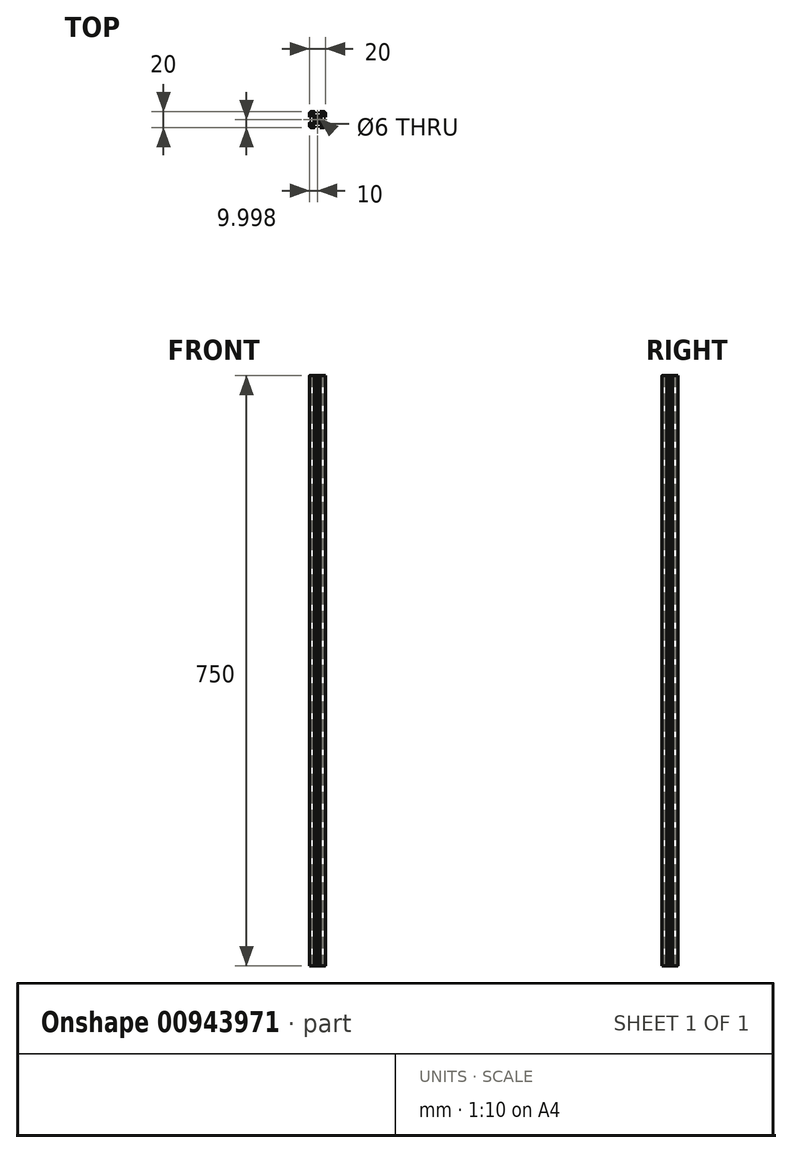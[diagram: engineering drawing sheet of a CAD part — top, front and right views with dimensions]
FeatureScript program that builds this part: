
annotation { "Feature Type Name" : "Feature", "Feature Type Description" : "" }
export const myFeature = defineFeature(function(context is Context, id is Id, definition is map)
    precondition{}
    {
        {
            var Q0;
            Q0=qCreatedBy(makeId("Top.planeOp"),FACE);
            var sketch = newSketch(context, id + "F0", { "sketchPlane" : qUnion([Q0])});
            skLineSegment(sketch, "E0.bottom", {"start": v(-8, -10) * mm, "end": v(8, -10) * mm});
            skLineSegment(sketch, "E0.top", {"start": v(-8, 10) * mm, "end": v(8, 10) * mm});
            skLineSegment(sketch, "E0.left", {"start": v(-10, -8) * mm, "end": v(-10, 8) * mm});
            skLineSegment(sketch, "E0.right", {"start": v(10, -8) * mm, "end": v(10, 8) * mm});
            skPoint(sketch, "E1.visualSharp", {"position": v(10, 10) * mm});
            skArc(sketch, "E1.filletArc", {"start": v(10, 8) * mm, "mid": v(9.41, 9.42) * mm, "end": v(8, 10) * mm});
            skPoint(sketch, "E2.visualSharp", {"position": v(-10, 10) * mm});
            skArc(sketch, "E2.filletArc", {"start": v(-8, 10) * mm, "mid": v(-9.41, 9.42) * mm, "end": v(-10, 8) * mm});
            skPoint(sketch, "E3.visualSharp", {"position": v(-10, -10) * mm});
            skArc(sketch, "E3.filletArc", {"start": v(-10, -8) * mm, "mid": v(-9.41, -9.4) * mm, "end": v(-8, -10) * mm});
            skPoint(sketch, "E4.visualSharp", {"position": v(10, -10) * mm});
            skArc(sketch, "E4.filletArc", {"start": v(8, -10) * mm, "mid": v(9.41, -9.4) * mm, "end": v(10, -8) * mm});
            skLineSegment(sketch, "E5", {"start": v(-10, -10) * mm, "end": v(10, 10) * mm, "construction": true});
            skLineSegment(sketch, "E6", {"start": v(-10, 10) * mm, "end": v(10, -10) * mm, "construction": true});
            skCircle(sketch, "E7", {"center": v(0, 0) * mm, "radius": 3 * mm});
            skCircle(sketch, "E8", {"center": v(0, 0) * mm, "radius": 2.75 * mm});
            skLineSegment(sketch, "E9.bottom", {"start": v(-2.45, -1.73) * mm, "end": v(-1.74, -2.44) * mm});
            skLineSegment(sketch, "E9.top", {"start": v(1.74, 2.45) * mm, "end": v(2.45, 1.75) * mm});
            skLineSegment(sketch, "E9.left", {"start": v(-2.45, -1.73) * mm, "end": v(1.74, 2.45) * mm});
            skLineSegment(sketch, "E9.right", {"start": v(-1.74, -2.44) * mm, "end": v(2.45, 1.75) * mm});
            skLineSegment(sketch, "E10.bottom", {"start": v(-2.45, 1.75) * mm, "end": v(-1.74, 2.45) * mm});
            skLineSegment(sketch, "E10.top", {"start": v(1.74, -2.44) * mm, "end": v(2.45, -1.73) * mm});
            skLineSegment(sketch, "E10.left", {"start": v(-2.45, 1.75) * mm, "end": v(1.74, -2.44) * mm});
            skLineSegment(sketch, "E10.right", {"start": v(-1.74, 2.45) * mm, "end": v(2.45, -1.73) * mm});
            skLineSegment(sketch, "E11", {"start": v(-3.5, 10) * mm, "end": v(-3.5, 9.5) * mm});
            skLineSegment(sketch, "E12", {"start": v(-3.5, 9.5) * mm, "end": v(-3, 9.5) * mm});
            skLineSegment(sketch, "E13", {"start": v(-3, 9.5) * mm, "end": v(-3, 8.5) * mm});
            skLineSegment(sketch, "E14", {"start": v(-3, 8.5) * mm, "end": v(-6, 8.5) * mm});
            skLineSegment(sketch, "E15", {"start": v(-6, 8.5) * mm, "end": v(-6, 7) * mm});
            skLineSegment(sketch, "E16", {"start": v(-3.5, 4.5) * mm, "end": v(-6, 7) * mm});
            skLineSegment(sketch, "E17", {"start": v(-3.5, 4.5) * mm, "end": v(3.5, 4.5) * mm});
            skLineSegment(sketch, "E18", {"start": v(3.5, 4.5) * mm, "end": v(6, 7) * mm});
            skLineSegment(sketch, "E19", {"start": v(6, 7) * mm, "end": v(6, 8.5) * mm});
            skLineSegment(sketch, "E20", {"start": v(6, 8.5) * mm, "end": v(3, 8.5) * mm});
            skLineSegment(sketch, "E21", {"start": v(3, 8.5) * mm, "end": v(3, 9.5) * mm});
            skLineSegment(sketch, "E22", {"start": v(3, 9.5) * mm, "end": v(3.5, 9.5) * mm});
            skLineSegment(sketch, "E23", {"start": v(3.5, 9.5) * mm, "end": v(3.5, 10) * mm});
            skLineSegment(sketch, "E24", {"start": v(0, 10) * mm, "end": v(0, -11.4) * mm, "construction": true});
            skLineSegment(sketch, "E25.1.0", {"start": v(-8.5, -6) * mm, "end": v(-7, -6) * mm});
            skLineSegment(sketch, "E25.1.1", {"start": v(-8.5, -3) * mm, "end": v(-8.5, -6) * mm});
            skLineSegment(sketch, "E25.1.2", {"start": v(-9.5, -3) * mm, "end": v(-8.5, -3) * mm});
            skLineSegment(sketch, "E25.1.3", {"start": v(-9.5, -3.5) * mm, "end": v(-9.5, -3) * mm});
            skLineSegment(sketch, "E25.1.4", {"start": v(-10, -3.5) * mm, "end": v(-9.5, -3.5) * mm});
            skLineSegment(sketch, "E25.1.5", {"start": v(-4.5, -3.5) * mm, "end": v(-7, -6) * mm});
            skLineSegment(sketch, "E25.1.6", {"start": v(-4.5, -3.5) * mm, "end": v(-4.5, 3.5) * mm});
            skLineSegment(sketch, "E25.1.7", {"start": v(-4.5, 3.5) * mm, "end": v(-7, 6) * mm});
            skLineSegment(sketch, "E25.1.8", {"start": v(-7, 6) * mm, "end": v(-8.5, 6) * mm});
            skLineSegment(sketch, "E25.1.9", {"start": v(-8.5, 6) * mm, "end": v(-8.5, 3) * mm});
            skLineSegment(sketch, "E25.1.10", {"start": v(-8.5, 3) * mm, "end": v(-9.5, 3) * mm});
            skLineSegment(sketch, "E25.1.11", {"start": v(-9.5, 3) * mm, "end": v(-9.5, 3.5) * mm});
            skLineSegment(sketch, "E25.1.12", {"start": v(-9.5, 3.5) * mm, "end": v(-10, 3.5) * mm});
            skLineSegment(sketch, "E25.2.0", {"start": v(6, -8.5) * mm, "end": v(6, -7) * mm});
            skLineSegment(sketch, "E25.2.1", {"start": v(3, -8.5) * mm, "end": v(6, -8.5) * mm});
            skLineSegment(sketch, "E25.2.2", {"start": v(3, -9.5) * mm, "end": v(3, -8.5) * mm});
            skLineSegment(sketch, "E25.2.3", {"start": v(3.5, -9.5) * mm, "end": v(3, -9.5) * mm});
            skLineSegment(sketch, "E25.2.4", {"start": v(3.5, -10) * mm, "end": v(3.5, -9.5) * mm});
            skLineSegment(sketch, "E25.2.5", {"start": v(3.5, -4.5) * mm, "end": v(6, -7) * mm});
            skLineSegment(sketch, "E25.2.6", {"start": v(3.5, -4.5) * mm, "end": v(-3.5, -4.5) * mm});
            skLineSegment(sketch, "E25.2.7", {"start": v(-3.5, -4.5) * mm, "end": v(-6, -7) * mm});
            skLineSegment(sketch, "E25.2.8", {"start": v(-6, -7) * mm, "end": v(-6, -8.5) * mm});
            skLineSegment(sketch, "E25.2.9", {"start": v(-6, -8.5) * mm, "end": v(-3, -8.5) * mm});
            skLineSegment(sketch, "E25.2.10", {"start": v(-3, -8.5) * mm, "end": v(-3, -9.5) * mm});
            skLineSegment(sketch, "E25.2.11", {"start": v(-3, -9.5) * mm, "end": v(-3.5, -9.5) * mm});
            skLineSegment(sketch, "E25.2.12", {"start": v(-3.5, -9.5) * mm, "end": v(-3.5, -10) * mm});
            skLineSegment(sketch, "E25.3.0", {"start": v(8.5, 6) * mm, "end": v(7, 6) * mm});
            skLineSegment(sketch, "E25.3.1", {"start": v(8.5, 3) * mm, "end": v(8.5, 6) * mm});
            skLineSegment(sketch, "E25.3.2", {"start": v(9.5, 3) * mm, "end": v(8.5, 3) * mm});
            skLineSegment(sketch, "E25.3.3", {"start": v(9.5, 3.5) * mm, "end": v(9.5, 3) * mm});
            skLineSegment(sketch, "E25.3.4", {"start": v(10, 3.5) * mm, "end": v(9.5, 3.5) * mm});
            skLineSegment(sketch, "E25.3.5", {"start": v(4.5, 3.5) * mm, "end": v(7, 6) * mm});
            skLineSegment(sketch, "E25.3.6", {"start": v(4.5, 3.5) * mm, "end": v(4.5, -3.5) * mm});
            skLineSegment(sketch, "E25.3.7", {"start": v(4.5, -3.5) * mm, "end": v(7, -6) * mm});
            skLineSegment(sketch, "E25.3.8", {"start": v(7, -6) * mm, "end": v(8.5, -6) * mm});
            skLineSegment(sketch, "E25.3.9", {"start": v(8.5, -6) * mm, "end": v(8.5, -3) * mm});
            skLineSegment(sketch, "E25.3.10", {"start": v(8.5, -3) * mm, "end": v(9.5, -3) * mm});
            skLineSegment(sketch, "E25.3.11", {"start": v(9.5, -3) * mm, "end": v(9.5, -3.5) * mm});
            skLineSegment(sketch, "E25.3.12", {"start": v(9.5, -3.5) * mm, "end": v(10, -3.5) * mm});
            skLineSegment(sketch, "E26", {"start": v(-0.5, 4.5) * mm, "end": v(0, 4) * mm});
            skLineSegment(sketch, "E27", {"start": v(0, 4) * mm, "end": v(0.5, 4.5) * mm});
            skLineSegment(sketch, "E28.1.0", {"start": v(-4, 0) * mm, "end": v(-4.5, 0.5) * mm});
            skLineSegment(sketch, "E28.1.1", {"start": v(-4.5, -0.5) * mm, "end": v(-4, 0) * mm});
            skLineSegment(sketch, "E28.2.0", {"start": v(0, -4) * mm, "end": v(-0.5, -4.5) * mm});
            skLineSegment(sketch, "E28.2.1", {"start": v(0.5, -4.5) * mm, "end": v(0, -4) * mm});
            skLineSegment(sketch, "E28.3.0", {"start": v(4, 0) * mm, "end": v(4.5, -0.5) * mm});
            skLineSegment(sketch, "E28.3.1", {"start": v(4.5, 0.5) * mm, "end": v(4, 0) * mm});
            skSolve(sketch);
        }
        {
            var Q0;
            {var subQ6=sQuery(id+"F0.wireOp",EDGE,"E1.filletArc");Q0=makeQuery(id+"F0.imprint","IMPRINT",FACE,{"disambiguationData":[TD([[makeQuery(id+"F0.imprint","IMPRINT",EDGE,{"derivedFrom":subQ6}),1.0]])]});}
            extrude(context, id + "F1", {"entities" : qUnion([Q0]), "depth" : 750 * mm, "offsetDistance" : 25.4 * mm});
        }
    });
